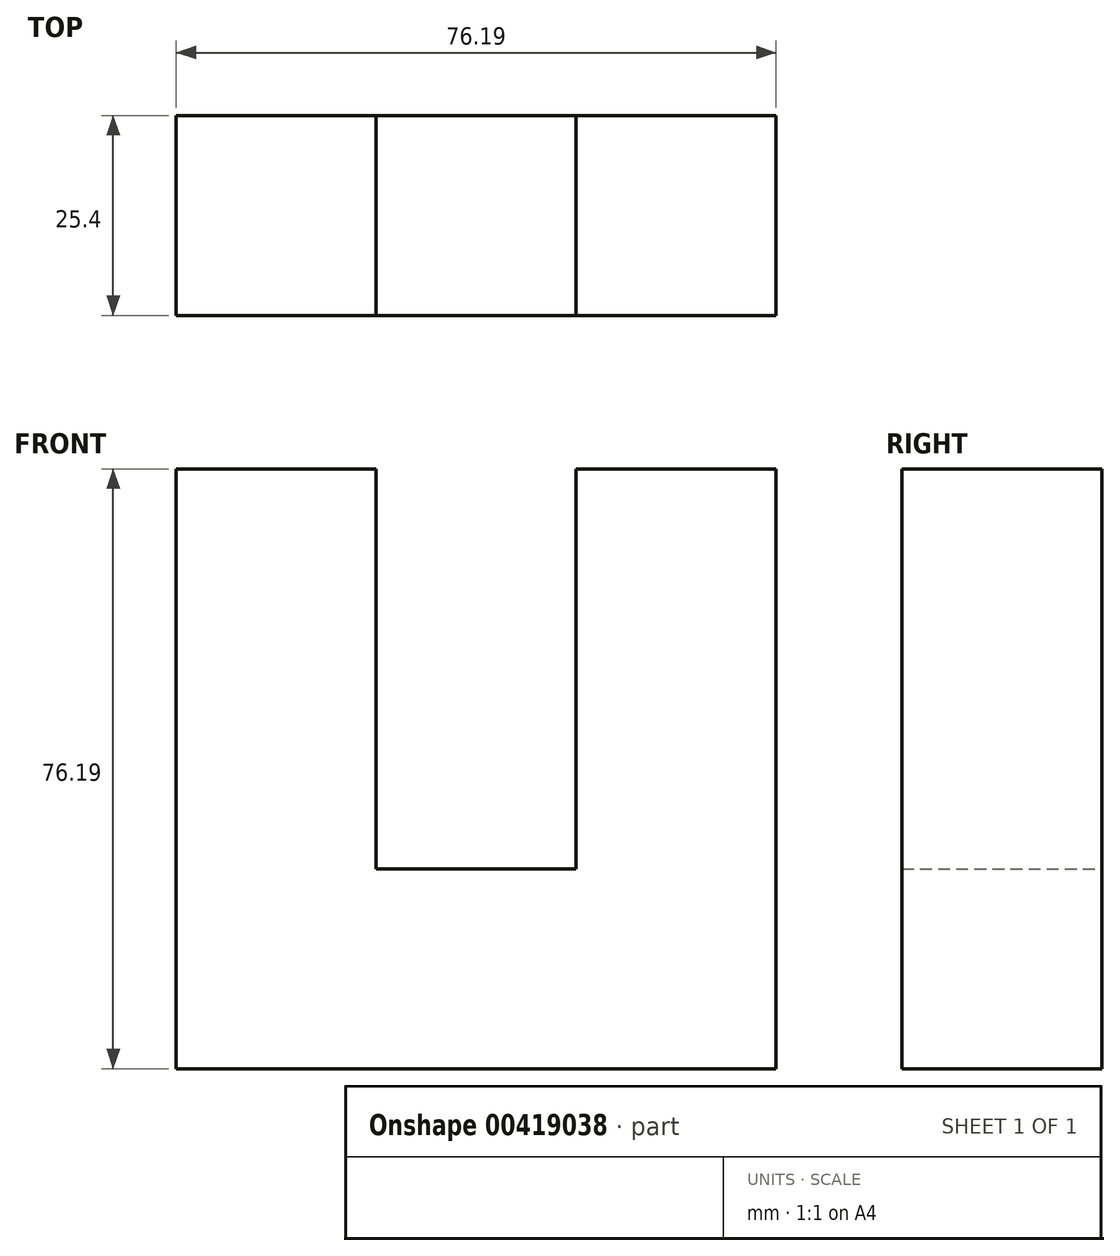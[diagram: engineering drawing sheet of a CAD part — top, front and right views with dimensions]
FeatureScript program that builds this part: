
annotation { "Feature Type Name" : "Feature", "Feature Type Description" : "" }
export const myFeature = defineFeature(function(context is Context, id is Id, definition is map)
    precondition{}
    {
        {
            var Q0;
            Q0=qCreatedBy(makeId("Front.planeOp"),FACE);
            var sketch = newSketch(context, id + "F0", { "sketchPlane" : qUnion([Q0])});
            skLineSegment(sketch, "E0", {"start": v(0, 0) * mm, "end": v(-76.2, 0) * mm});
            skLineSegment(sketch, "E1", {"start": v(-76.2, 0) * mm, "end": v(-76.2, 76.2) * mm});
            skLineSegment(sketch, "E2", {"start": v(-76.2, 76.2) * mm, "end": v(-50.8, 76.2) * mm});
            skLineSegment(sketch, "E3", {"start": v(-50.8, 76.2) * mm, "end": v(-50.8, 25.4) * mm});
            skLineSegment(sketch, "E4", {"start": v(-50.8, 25.4) * mm, "end": v(-25.4, 25.4) * mm});
            skLineSegment(sketch, "E5", {"start": v(-25.4, 25.4) * mm, "end": v(-25.4, 76.2) * mm});
            skLineSegment(sketch, "E6", {"start": v(-25.4, 76.2) * mm, "end": v(0, 76.2) * mm});
            skLineSegment(sketch, "E7", {"start": v(0, 76.2) * mm, "end": v(0, 0) * mm});
            skSolve(sketch);
        }
        {
            var Q0;
            Q0=makeQuery(id+"F0.imprint","IMPRINT",FACE,{"disambiguationData":[TD([[makeQuery(id+"F0.imprint","IMPRINT",EDGE,{"derivedFrom":sQuery(id+"F0.wireOp",EDGE,"E0")}),-1.0]])]});
            extrude(context, id + "F1", {"entities" : qUnion([Q0]), "depth" : 25.4 * mm});
        }
    });
